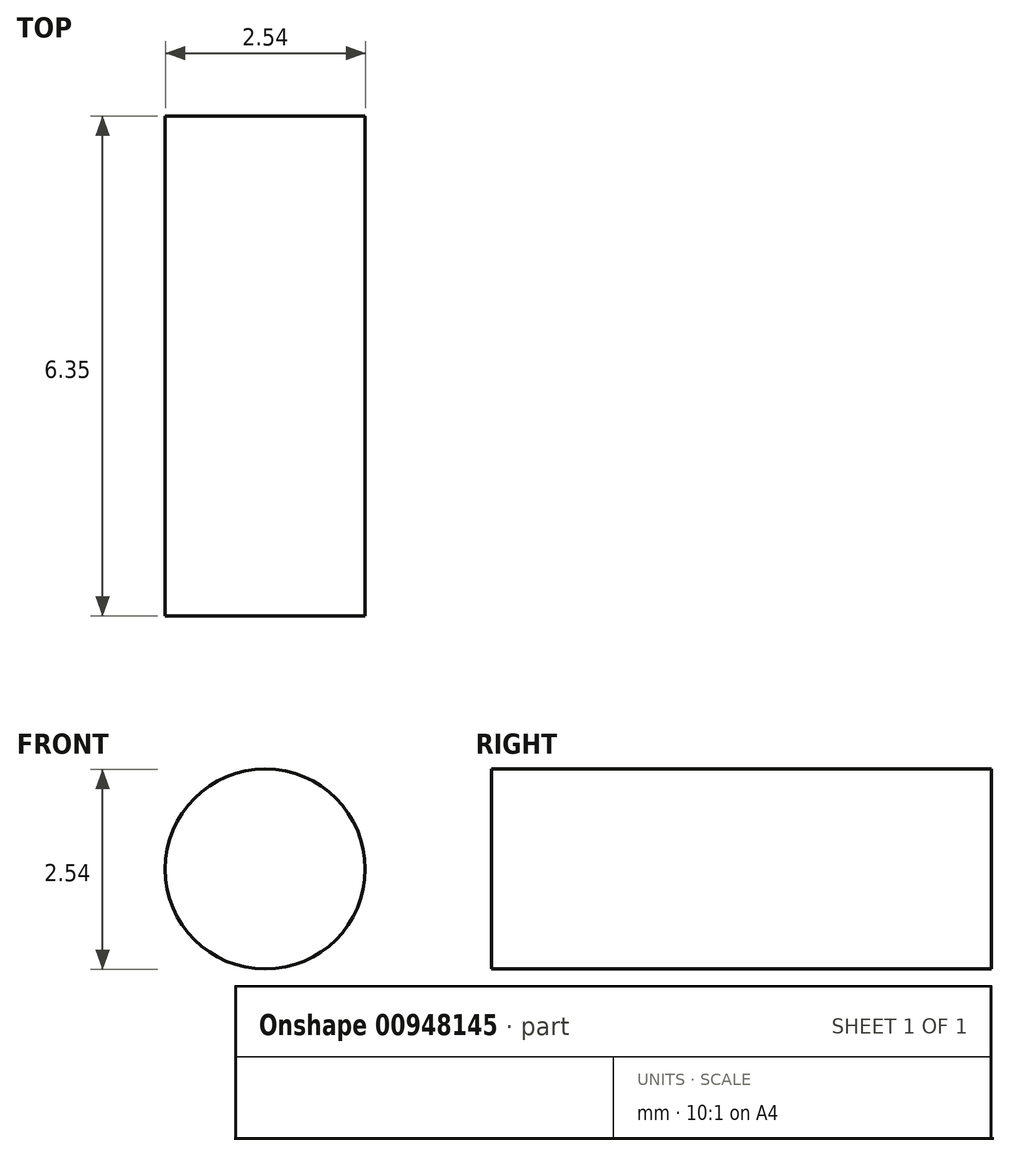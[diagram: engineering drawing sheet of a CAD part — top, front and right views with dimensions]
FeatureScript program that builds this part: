
annotation { "Feature Type Name" : "Feature", "Feature Type Description" : "" }
export const myFeature = defineFeature(function(context is Context, id is Id, definition is map)
    precondition{}
    {
        {
            var Q0;
            Q0=qCreatedBy(makeId("Front.planeOp"),FACE);
            var sketch = newSketch(context, id + "F0", { "sketchPlane" : qUnion([Q0])});
            skCircle(sketch, "E0", {"center": v(-41.58, 25.5) * mm, "radius": 1.27 * mm});
            skSolve(sketch);
        }
        {
            var Q0;
            Q0=makeQuery(id+"F0.imprint","IMPRINT",FACE,{"disambiguationData":[TD([[makeQuery(id+"F0.imprint","IMPRINT",EDGE,{"derivedFrom":sQuery(id+"F0.wireOp",EDGE,"E0")}),1.0]])]});
            extrude(context, id + "F1", {"entities" : qUnion([Q0]), "depth" : 6.35 * mm, "offsetDistance" : 25.4 * mm});
        }
    });
